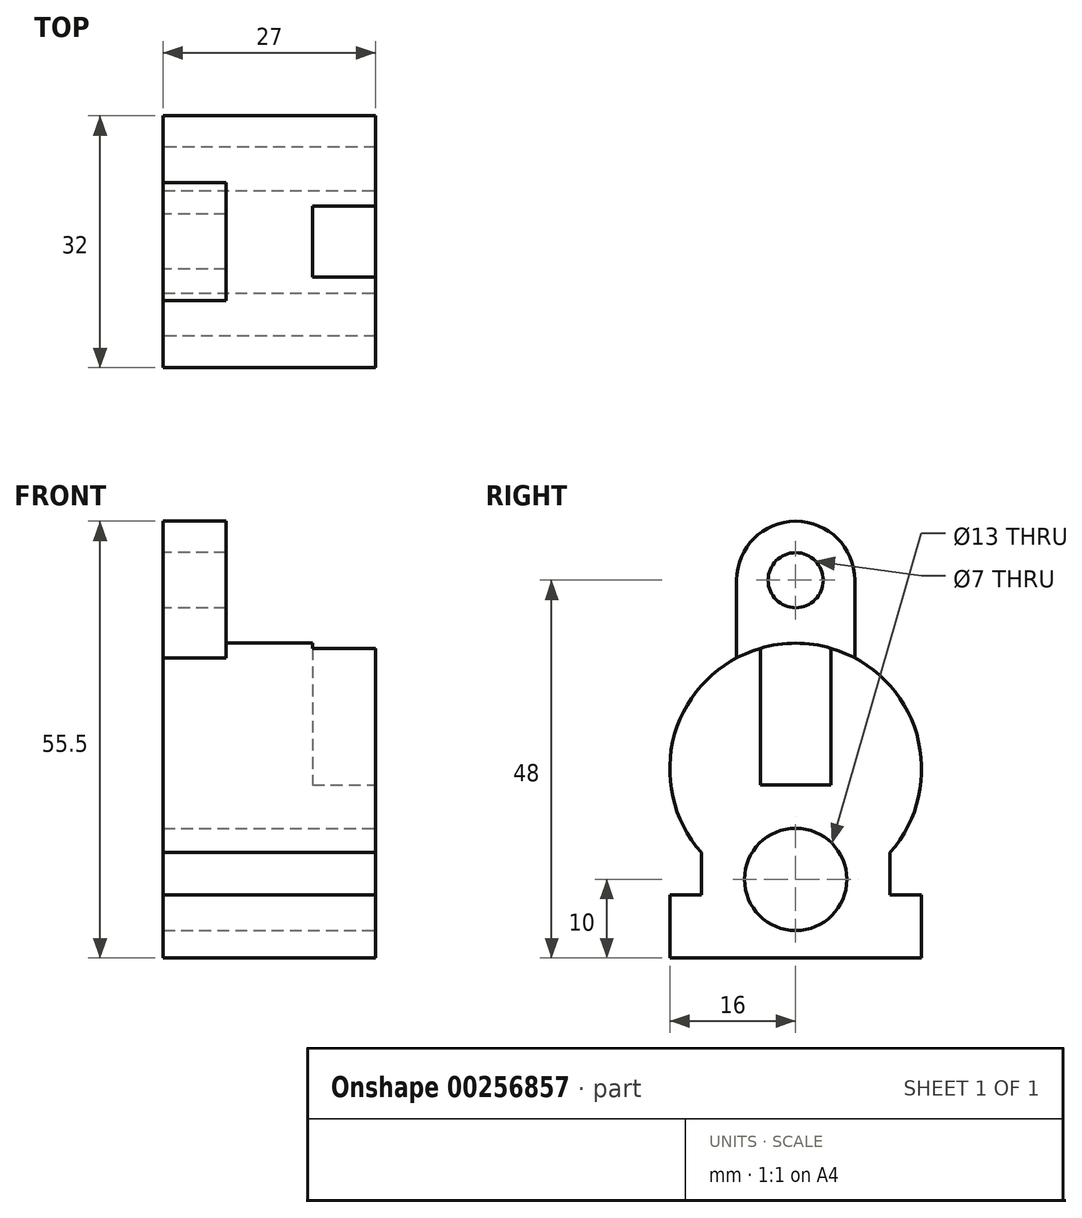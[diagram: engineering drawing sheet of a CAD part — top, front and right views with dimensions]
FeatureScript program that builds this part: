
annotation { "Feature Type Name" : "Feature", "Feature Type Description" : "" }
export const myFeature = defineFeature(function(context is Context, id is Id, definition is map)
    precondition{}
    {
        {
            var Q0;
            Q0=qCreatedBy(makeId("Right.planeOp"),FACE);
            var sketch = newSketch(context, id + "F0", { "sketchPlane" : qUnion([Q0])});
            skLineSegment(sketch, "E0.bottom", {"start": v(16, 24) * mm, "end": v(-16, 24) * mm});
            skLineSegment(sketch, "E0.top", {"start": v(16, -24) * mm, "end": v(-16, -24) * mm});
            skLineSegment(sketch, "E0.left", {"start": v(16, 24) * mm, "end": v(16, -24) * mm});
            skLineSegment(sketch, "E0.right", {"start": v(-16, 24) * mm, "end": v(-16, -24) * mm});
            skPoint(sketch, "E0.middle", {"position": v(0, 0) * mm});
            skLineSegment(sketch, "E1", {"start": v(-16, -16) * mm, "end": v(16, -16) * mm});
            skLineSegment(sketch, "E2", {"start": v(12, 24) * mm, "end": v(12, -24) * mm});
            skLineSegment(sketch, "E3", {"start": v(-12, 24) * mm, "end": v(-12, -24) * mm});
            skLineSegment(sketch, "E4", {"start": v(-16, 0) * mm, "end": v(16, 0) * mm});
            skCircle(sketch, "E5", {"center": v(0, 0) * mm, "radius": 16 * mm});
            skSolve(sketch);
        }
        {
            var Q0;
            {var subQ0=sQuery(id+"F0.wireOp",EDGE,"E5");var subQ1=sQuery(id+"F0.wireOp",EDGE,"E2");var subQ2=makeQuery(id+"F0.imprint","INTERSECT",VERTEX,{"disambiguationData":[OD(0.0)],"derivedFrom":[subQ1,subQ0]});Q0=makeQuery(id+"F0.imprint","IMPRINT",FACE,{"disambiguationData":[TD([[makeQuery(id+"F0.imprint","IMPRINT",EDGE,{"disambiguationData":[TD([[subQ2,-1.0]])],"derivedFrom":subQ1}),-1.0]])]});}
            var Q1;
            {var subQ0=sQuery(id+"F0.wireOp",EDGE,"E5");var subQ1=sQuery(id+"F0.wireOp",EDGE,"E2");var subQ2=makeQuery(id+"F0.imprint","INTERSECT",VERTEX,{"disambiguationData":[OD(0.0)],"derivedFrom":[subQ1,subQ0]});Q1=makeQuery(id+"F0.imprint","IMPRINT",FACE,{"disambiguationData":[TD([[makeQuery(id+"F0.imprint","IMPRINT",EDGE,{"disambiguationData":[TD([[subQ2,-1.0]])],"derivedFrom":subQ1}),1.0]])]});}
            var Q2;
            {var subQ0=sQuery(id+"F0.wireOp",EDGE,"E4");var subQ1=sQuery(id+"F0.wireOp",EDGE,"E2");var subQ2=makeQuery(id+"F0.imprint","INTERSECT",VERTEX,{"derivedFrom":[subQ1,subQ0]});Q2=makeQuery(id+"F0.imprint","IMPRINT",FACE,{"disambiguationData":[TD([[makeQuery(id+"F0.imprint","IMPRINT",EDGE,{"disambiguationData":[TD([[subQ2,-1.0]])],"derivedFrom":subQ1}),-1.0]])]});}
            var Q3;
            {var subQ0=sQuery(id+"F0.wireOp",EDGE,"E4");var subQ1=sQuery(id+"F0.wireOp",EDGE,"E2");var subQ2=makeQuery(id+"F0.imprint","INTERSECT",VERTEX,{"derivedFrom":[subQ1,subQ0]});Q3=makeQuery(id+"F0.imprint","IMPRINT",FACE,{"disambiguationData":[TD([[makeQuery(id+"F0.imprint","IMPRINT",EDGE,{"disambiguationData":[TD([[subQ2,-1.0]])],"derivedFrom":subQ1}),1.0]])]});}
            var Q4;
            {var subQ0=sQuery(id+"F0.wireOp",EDGE,"E5");var subQ1=sQuery(id+"F0.wireOp",EDGE,"E3");var subQ2=makeQuery(id+"F0.imprint","INTERSECT",VERTEX,{"disambiguationData":[OD(0.0)],"derivedFrom":[subQ1,subQ0]});Q4=makeQuery(id+"F0.imprint","IMPRINT",FACE,{"disambiguationData":[TD([[makeQuery(id+"F0.imprint","IMPRINT",EDGE,{"disambiguationData":[TD([[subQ2,-1.0]])],"derivedFrom":subQ1}),-1.0]])]});}
            var Q5;
            {var subQ0=sQuery(id+"F0.wireOp",EDGE,"E4");var subQ1=sQuery(id+"F0.wireOp",EDGE,"E3");var subQ2=makeQuery(id+"F0.imprint","INTERSECT",VERTEX,{"derivedFrom":[subQ1,subQ0]});Q5=makeQuery(id+"F0.imprint","IMPRINT",FACE,{"disambiguationData":[TD([[makeQuery(id+"F0.imprint","IMPRINT",EDGE,{"disambiguationData":[TD([[subQ2,-1.0]])],"derivedFrom":subQ1}),-1.0]])]});}
            var Q6;
            {var subQ0=sQuery(id+"F0.wireOp",EDGE,"E3");var subQ1=sQuery(id+"F0.wireOp",EDGE,"E1");var subQ2=makeQuery(id+"F0.imprint","INTERSECT",VERTEX,{"derivedFrom":[subQ1,subQ0]});Q6=makeQuery(id+"F0.imprint","IMPRINT",FACE,{"disambiguationData":[TD([[makeQuery(id+"F0.imprint","IMPRINT",EDGE,{"disambiguationData":[TD([[subQ2,-1.0]])],"derivedFrom":subQ1}),1.0]])]});}
            var Q7;
            {var subQ2=sQuery(id+"F0.wireOp",EDGE,"E2");var subQ5=sQuery(id+"F0.wireOp",EDGE,"E0.top");var subQ8=makeQuery(id+"F0.imprint","INTERSECT",VERTEX,{"derivedFrom":[subQ5,subQ2]});Q7=makeQuery(id+"F0.imprint","IMPRINT",FACE,{"disambiguationData":[TD([[makeQuery(id+"F0.imprint","IMPRINT",EDGE,{"disambiguationData":[TD([[subQ8,-1.0]])],"derivedFrom":subQ5}),-1.0]])]});}
            var Q8;
            {var subQ0=sQuery(id+"F0.wireOp",EDGE,"E0.right");var subQ1=sQuery(id+"F0.wireOp",EDGE,"E0.top");var subQ2=makeQuery(id+"F0.imprint","INTERSECT",VERTEX,{"derivedFrom":[subQ1,subQ0]});Q8=makeQuery(id+"F0.imprint","IMPRINT",FACE,{"disambiguationData":[TD([[makeQuery(id+"F0.imprint","IMPRINT",EDGE,{"disambiguationData":[TD([[subQ2,1.0]])],"derivedFrom":subQ1}),-1.0]])]});}
            var Q9;
            {var subQ0=sQuery(id+"F0.wireOp",EDGE,"E5");var subQ1=sQuery(id+"F0.wireOp",EDGE,"E1");var subQ2=makeQuery(id+"F0.imprint","INTERSECT",VERTEX,{"derivedFrom":[subQ1,subQ0]});Q9=makeQuery(id+"F0.imprint","IMPRINT",FACE,{"disambiguationData":[TD([[makeQuery(id+"F0.imprint","IMPRINT",EDGE,{"disambiguationData":[TD([[subQ2,-1.0]])],"derivedFrom":subQ1}),1.0]])]});}
            var Q10;
            {var subQ0=sQuery(id+"F0.wireOp",EDGE,"E0.left");var subQ1=sQuery(id+"F0.wireOp",EDGE,"E0.top");var subQ2=makeQuery(id+"F0.imprint","INTERSECT",VERTEX,{"derivedFrom":[subQ1,subQ0]});Q10=makeQuery(id+"F0.imprint","IMPRINT",FACE,{"disambiguationData":[TD([[makeQuery(id+"F0.imprint","IMPRINT",EDGE,{"disambiguationData":[TD([[subQ2,-1.0]])],"derivedFrom":subQ1}),-1.0]])]});}
            extrude(context, id + "F1", {"entities" : qUnion([Q0, Q1, Q2, Q3, Q4, Q5, Q6, Q7, Q8, Q9, Q10]), "endBound" : BoundingType.SYMMETRIC, "depth" : 27 * mm});
        }
        {
            var Q0;
            Q0=makeQuery(id+"F1.opExtrude","CAP_FACE",FACE,{"disambiguationData":[OSD([sQuery(id+"F0.wireOp",EDGE,"E0.top"),sQuery(id+"F0.wireOp",EDGE,"E0.left"),sQuery(id+"F0.wireOp",EDGE,"E0.right"),sQuery(id+"F0.wireOp",EDGE,"E1"),sQuery(id+"F0.wireOp",EDGE,"E2"),sQuery(id+"F0.wireOp",EDGE,"E3"),sQuery(id+"F0.wireOp",EDGE,"E5")])],"isStart":false});
            var sketch = newSketch(context, id + "F2", { "sketchPlane" : qUnion([Q0])});
            skLineSegment(sketch, "E6.bottom", {"start": v(16, 24) * mm, "end": v(-16, 24) * mm});
            skLineSegment(sketch, "E6.top", {"start": v(16, -24) * mm, "end": v(-16, -24) * mm});
            skLineSegment(sketch, "E6.left", {"start": v(16, 24) * mm, "end": v(16, -24) * mm});
            skLineSegment(sketch, "E6.right", {"start": v(-16, 24) * mm, "end": v(-16, -24) * mm});
            skPoint(sketch, "E6.middle", {"position": v(0, 0) * mm});
            skLineSegment(sketch, "E7", {"start": v(-16, -14) * mm, "end": v(16, -14) * mm});
            skPoint(sketch, "E8", {"position": v(0, -14) * mm});
            skSolve(sketch);
        }
        {
            var Q0;
            Q0=sQuery(id+"F2.wireOp",VERTEX,"E8");
            var Q1;
            Q1=makeQuery(id+"F1.opExtrude","SWEPT_BODY",BODY,{"disambiguationData":[OSD([sQuery(id+"F0.wireOp",EDGE,"E0.top"),sQuery(id+"F0.wireOp",EDGE,"E0.left"),sQuery(id+"F0.wireOp",EDGE,"E0.right"),sQuery(id+"F0.wireOp",EDGE,"E1"),sQuery(id+"F0.wireOp",EDGE,"E2"),sQuery(id+"F0.wireOp",EDGE,"E3"),sQuery(id+"F0.wireOp",EDGE,"E5")])]});
            hole(context, id + "F3", {"style" : HoleStyle.SIMPLE, "endStyle" : HoleEndStyle.THROUGH, "holeDiameter" : 13 * mm, "tappedDepth" : 12 * mm, "tapClearance" : 3, "locations" : qUnion([Q0]), "scope" : qUnion([Q1])});
        }
        {
            var Q0;
            Q0=qCreatedBy(makeId("Top.planeOp"),FACE);
            var sketch = newSketch(context, id + "F4", { "sketchPlane" : qUnion([Q0])});
            skLineSegment(sketch, "E9.bottom", {"start": v(-13.5, 16) * mm, "end": v(13.5, 16) * mm});
            skLineSegment(sketch, "E9.top", {"start": v(-13.5, -16) * mm, "end": v(13.5, -16) * mm});
            skLineSegment(sketch, "E9.left", {"start": v(-13.5, 16) * mm, "end": v(-13.5, -16) * mm});
            skLineSegment(sketch, "E9.right", {"start": v(13.5, 16) * mm, "end": v(13.5, -16) * mm});
            skPoint(sketch, "E9.middle", {"position": v(0, 0) * mm});
            skLineSegment(sketch, "E10", {"start": v(5.5, -16) * mm, "end": v(5.5, 16) * mm});
            skLineSegment(sketch, "E11", {"start": v(-13.5, 4.5) * mm, "end": v(13.5, 4.5) * mm});
            skPoint(sketch, "E11.endSnap0", {"position": v(13.5, 0) * mm});
            skLineSegment(sketch, "E12", {"start": v(-13.5, -4.5) * mm, "end": v(13.5, -4.5) * mm});
            skLineSegment(sketch, "E13", {"start": v(-13.5, 7.5) * mm, "end": v(13.5, 7.5) * mm});
            skLineSegment(sketch, "E14", {"start": v(-13.5, -7.5) * mm, "end": v(13.5, -7.5) * mm});
            skLineSegment(sketch, "E15", {"start": v(-5.5, -16) * mm, "end": v(-5.5, 16) * mm});
            skSolve(sketch);
        }
        {
            var Q0;
            {var subQ0=sQuery(id+"F4.wireOp",EDGE,"E11");var subQ1=sQuery(id+"F4.wireOp",EDGE,"E9.left");var subQ2=makeQuery(id+"F4.imprint","INTERSECT",VERTEX,{"derivedFrom":[subQ1,subQ0]});Q0=makeQuery(id+"F4.imprint","IMPRINT",FACE,{"disambiguationData":[TD([[makeQuery(id+"F4.imprint","IMPRINT",EDGE,{"disambiguationData":[TD([[subQ2,-1.0]])],"derivedFrom":subQ1}),1.0]])]});}
            var Q1;
            {var subQ0=sQuery(id+"F4.wireOp",EDGE,"E11");var subQ1=sQuery(id+"F4.wireOp",EDGE,"E9.left");var subQ2=makeQuery(id+"F4.imprint","INTERSECT",VERTEX,{"derivedFrom":[subQ1,subQ0]});Q1=makeQuery(id+"F4.imprint","IMPRINT",FACE,{"disambiguationData":[TD([[makeQuery(id+"F4.imprint","IMPRINT",EDGE,{"disambiguationData":[TD([[subQ2,1.0]])],"derivedFrom":subQ1}),1.0]])]});}
            var Q2;
            {var subQ0=sQuery(id+"F4.wireOp",EDGE,"E12");var subQ1=sQuery(id+"F4.wireOp",EDGE,"E9.left");var subQ2=makeQuery(id+"F4.imprint","INTERSECT",VERTEX,{"derivedFrom":[subQ1,subQ0]});Q2=makeQuery(id+"F4.imprint","IMPRINT",FACE,{"disambiguationData":[TD([[makeQuery(id+"F4.imprint","IMPRINT",EDGE,{"disambiguationData":[TD([[subQ2,-1.0]])],"derivedFrom":subQ1}),1.0]])]});}
            extrude(context, id + "F5", {"entities" : qUnion([Q0, Q1, Q2]), "operationType" : NewBodyOperationType.ADD, "depth" : 31.5 * mm});
        }
        {
            var Q0;
            {var subQ0=sQuery(id+"F4.wireOp",EDGE,"E11");var subQ1=sQuery(id+"F4.wireOp",EDGE,"E9.right");var subQ2=makeQuery(id+"F4.imprint","INTERSECT",VERTEX,{"derivedFrom":[subQ1,subQ0]});Q0=makeQuery(id+"F4.imprint","IMPRINT",FACE,{"disambiguationData":[TD([[makeQuery(id+"F4.imprint","IMPRINT",EDGE,{"disambiguationData":[TD([[subQ2,-1.0]])],"derivedFrom":subQ1}),-1.0]])]});}
            extrude(context, id + "F6", {"entities" : qUnion([Q0]), "operationType" : NewBodyOperationType.REMOVE, "depth" : 110 * mm, "hasSecondDirection" : true, "secondDirectionOppositeDirection" : true, "secondDirectionDepth" : 2 * mm});
        }
        {
            var Q0;
            Q0=makeQuery(id+"F5.boolean.opBoolean","MERGE",FACE,{"derivedFrom":[makeQuery(id+"F1.opExtrude","CAP_FACE",FACE,{"disambiguationData":[OSD([sQuery(id+"F0.wireOp",EDGE,"E0.top"),sQuery(id+"F0.wireOp",EDGE,"E0.left"),sQuery(id+"F0.wireOp",EDGE,"E0.right"),sQuery(id+"F0.wireOp",EDGE,"E1"),sQuery(id+"F0.wireOp",EDGE,"E2"),sQuery(id+"F0.wireOp",EDGE,"E3"),sQuery(id+"F0.wireOp",EDGE,"E5")])],"isStart":true}),makeQuery(id+"F5.opExtrude","SWEPT_FACE",FACE,{"disambiguationData":[OSD([sQuery(id+"F4.wireOp",EDGE,"E9.left")])]})]});
            var sketch = newSketch(context, id + "F7", { "sketchPlane" : qUnion([Q0])});
            skLineSegment(sketch, "E16.bottom", {"start": v(16, 31.5) * mm, "end": v(-16, 31.5) * mm});
            skLineSegment(sketch, "E16.top", {"start": v(16, -31.5) * mm, "end": v(-16, -31.5) * mm});
            skLineSegment(sketch, "E16.left", {"start": v(16, 31.5) * mm, "end": v(16, -31.5) * mm});
            skLineSegment(sketch, "E16.right", {"start": v(-16, 31.5) * mm, "end": v(-16, -31.5) * mm});
            skPoint(sketch, "E16.middle", {"position": v(0, 0) * mm});
            skLineSegment(sketch, "E17", {"start": v(-16, 24) * mm, "end": v(16, 24) * mm});
            skArc(sketch, "E18", {"start": v(7.5, 24) * mm, "mid": v(0, 31.5) * mm, "end": v(-7.5, 24) * mm});
            skSolve(sketch);
        }
        {
            var Q0;
            Q0=sQuery(id+"F7.wireOp",VERTEX,"E18.center");
            var Q1;
            Q1=makeQuery(id+"F1.opExtrude","SWEPT_BODY",BODY,{"disambiguationData":[OSD([sQuery(id+"F0.wireOp",EDGE,"E0.top"),sQuery(id+"F0.wireOp",EDGE,"E0.left"),sQuery(id+"F0.wireOp",EDGE,"E0.right"),sQuery(id+"F0.wireOp",EDGE,"E1"),sQuery(id+"F0.wireOp",EDGE,"E2"),sQuery(id+"F0.wireOp",EDGE,"E3"),sQuery(id+"F0.wireOp",EDGE,"E5")])]});
            hole(context, id + "F8", {"style" : HoleStyle.SIMPLE, "endStyle" : HoleEndStyle.THROUGH, "holeDiameter" : 7 * mm, "tappedDepth" : 12 * mm, "tapClearance" : 3, "locations" : qUnion([Q0]), "scope" : qUnion([Q1])});
        }
        {
            var Q0;
            {var subQ0=sQuery(id+"F7.wireOp",EDGE,"E16.bottom");var subQ3=sQuery(id+"F7.wireOp",EDGE,"E18");var subQ4=makeQuery(id+"F7.imprint","INTERSECT",VERTEX,{"derivedFrom":[subQ0,subQ3]});Q0=makeQuery(id+"F7.imprint","IMPRINT",FACE,{"disambiguationData":[TD([[makeQuery(id+"F7.imprint","IMPRINT",EDGE,{"disambiguationData":[TD([[subQ4,-1.0]])],"derivedFrom":subQ0}),-1.0]])]});}
            var Q1;
            {var subQ0=sQuery(id+"F7.wireOp",EDGE,"E16.bottom");var subQ3=sQuery(id+"F7.wireOp",EDGE,"E18");var subQ4=makeQuery(id+"F7.imprint","INTERSECT",VERTEX,{"derivedFrom":[subQ0,subQ3]});Q1=makeQuery(id+"F7.imprint","IMPRINT",FACE,{"disambiguationData":[TD([[makeQuery(id+"F7.imprint","IMPRINT",EDGE,{"disambiguationData":[TD([[subQ4,1.0]])],"derivedFrom":subQ0}),-1.0]])]});}
            extrude(context, id + "F9", {"entities" : qUnion([Q0, Q1]), "operationType" : NewBodyOperationType.REMOVE, "oppositeDirection" : true, "depth" : 25 * mm});
        }
    });
